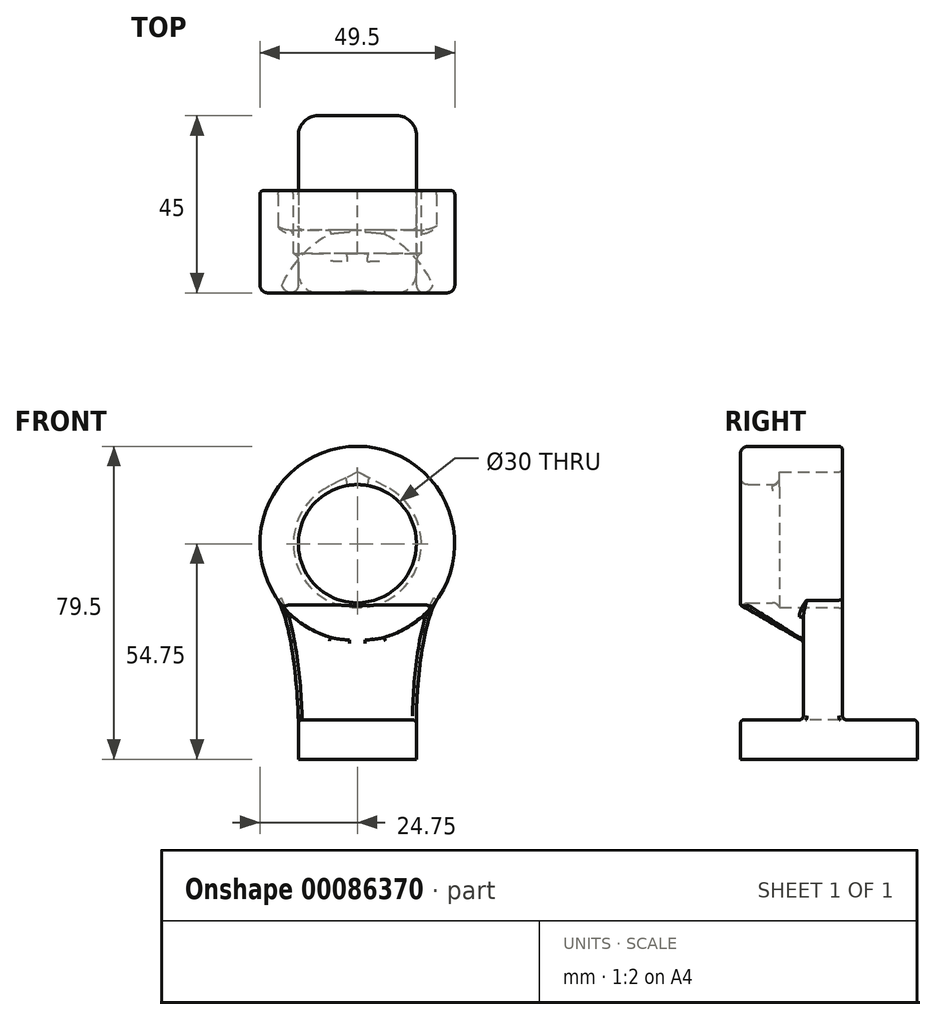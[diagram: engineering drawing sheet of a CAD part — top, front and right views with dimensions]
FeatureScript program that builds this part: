
annotation { "Feature Type Name" : "Feature", "Feature Type Description" : "" }
export const myFeature = defineFeature(function(context is Context, id is Id, definition is map)
    precondition{}
    {
        {
            var Q0;
            Q0=qCreatedBy(makeId("Front.planeOp"),FACE);
            var sketch = newSketch(context, id + "F0", { "sketchPlane" : qUnion([Q0])});
            skCircle(sketch, "E0", {"center": v(0, 54.75) * mm, "radius": 24.75 * mm});
            skLineSegment(sketch, "E1", {"start": v(-15, 0) * mm, "end": v(0, 0) * mm});
            skLineSegment(sketch, "E2", {"start": v(0, 0) * mm, "end": v(15, 0) * mm});
            skLineSegment(sketch, "E3", {"start": v(15, 0) * mm, "end": v(15, 10) * mm});
            skLineSegment(sketch, "E4", {"start": v(15, 10) * mm, "end": v(-15, 10) * mm});
            skLineSegment(sketch, "E5", {"start": v(-15, 10) * mm, "end": v(-15, 0) * mm});
            skFitSpline(sketch, "E6", {"points": [v(-15, 10) * mm, v(-20.17, 40.4) * mm], "startDerivative": vector(-0.6, 19.25) * mm, "endDerivative": vector(-11.77, 21.87) * mm});
            skFitSpline(sketch, "E7", {"points": [v(15, 10) * mm, v(20.17, 40.4) * mm], "startDerivative": vector(-0.15, 19.91) * mm, "endDerivative": vector(11.86, 18.55) * mm});
            skCircle(sketch, "E8", {"center": v(0, 54.75) * mm, "radius": 40 * mm, "construction": true});
            skSolve(sketch);
        }
        {
            var Q0;
            Q0 = qSketchRegion(id + "F0", true);
            extrude(context, id + "F1", {"entities" : qUnion([Q0]), "oppositeDirection" : true, "depth" : 10 * mm, "offsetDistance" : 25 * mm});
        }
        {
            var Q0;
            {var subQ0=sQuery(id+"F0.wireOp",EDGE,"E0");var subQ1=makeQuery(id+"F0.imprint","INTERSECT",VERTEX,{"derivedFrom":[subQ0,sQuery(id+"F0.wireOp",EDGE,"E6")]});Q0=makeQuery(id+"F0.imprint","IMPRINT",FACE,{"disambiguationData":[TD([[makeQuery(id+"F0.imprint","IMPRINT",EDGE,{"disambiguationData":[TD([[subQ1,-1.0]])],"derivedFrom":subQ0}),1.0]])]});}
            var Q1;
            Q1=makeQuery(id+"F0.imprint","IMPRINT",FACE,{"disambiguationData":[TD([[makeQuery(id+"F0.imprint","IMPRINT",EDGE,{"derivedFrom":sQuery(id+"F0.wireOp",EDGE,"E1")}),1.0]])]});
            extrude(context, id + "F2", {"entities" : qUnion([Q0, Q1]), "operationType" : NewBodyOperationType.ADD, "depth" : 16 * mm, "offsetDistance" : 25 * mm});
        }
        {
            var Q0;
            {var subQ0=sQuery(id+"F0.wireOp",EDGE,"E3");Q0=makeQuery(id+"F2.boolean.opBoolean","MERGE",FACE,{"derivedFrom":[makeQuery(id+"F1.opExtrude","SWEPT_FACE",FACE,{"disambiguationData":[OSD([subQ0])]}),makeQuery(id+"F2.opExtrude","SWEPT_FACE",FACE,{"disambiguationData":[OSD([subQ0])]})]});}
            var sketch = newSketch(context, id + "F3", { "sketchPlane" : qUnion([Q0])});
            skLineSegment(sketch, "E9.0", {"start": v(-16, 30) * mm, "end": v(-16, 79.5) * mm});
            skLineSegment(sketch, "E10.0", {"start": v(0, 30) * mm, "end": v(0, 79.5) * mm});
            skLineSegment(sketch, "E11", {"start": v(0, 30) * mm, "end": v(-16, 39.24) * mm});
            skLineSegment(sketch, "E12.0", {"start": v(-16, 10) * mm, "end": v(0, 10) * mm});
            skLineSegment(sketch, "E13", {"start": v(-16, 30) * mm, "end": v(0, 30) * mm});
            skSolve(sketch);
        }
        {
            var Q0;
            {var subQ2=sQuery(id+"F3.wireOp",EDGE,"E11");Q0=makeQuery(id+"F3.imprint","IMPRINT",FACE,{"disambiguationData":[TD([[makeQuery(id+"F3.imprint","IMPRINT",EDGE,{"derivedFrom":subQ2}),1.0]])]});}
            extrude(context, id + "F4", {"entities" : qUnion([Q0]), "operationType" : NewBodyOperationType.REMOVE, "endBound" : BoundingType.THROUGH_ALL, "oppositeDirection" : true, "depth" : 25 * mm, "offsetDistance" : 25 * mm, "hasSecondDirection" : true, "secondDirectionBound" : SecondDirectionBoundingType.THROUGH_ALL, "secondDirectionOppositeDirection" : false, "secondDirectionDepth" : 25 * mm});
        }
        {
            var Q0;
            Q0=makeQuery(id+"F1.opExtrude","CAP_FACE",FACE,{"disambiguationData":[OSD([sQuery(id+"F0.wireOp",EDGE,"E0"),sQuery(id+"F0.wireOp",EDGE,"E1"),sQuery(id+"F0.wireOp",EDGE,"E2"),sQuery(id+"F0.wireOp",EDGE,"E3"),sQuery(id+"F0.wireOp",EDGE,"E5"),sQuery(id+"F0.wireOp",EDGE,"E6"),sQuery(id+"F0.wireOp",EDGE,"E7")])],"isStart":false});
            var sketch = newSketch(context, id + "F5", { "sketchPlane" : qUnion([Q0])});
            skCircle(sketch, "E14", {"center": v(0, 54.75) * mm, "radius": 15 * mm});
            skSolve(sketch);
        }
        {
            var Q0;
            Q0 = qSketchRegion(id + "F5", true);
            extrude(context, id + "F6", {"entities" : qUnion([Q0]), "operationType" : NewBodyOperationType.REMOVE, "endBound" : BoundingType.THROUGH_ALL, "oppositeDirection" : true, "depth" : 25 * mm, "offsetDistance" : 25 * mm});
        }
        {
            var Q0;
            Q0=makeQuery(id+"F1.opExtrude","CAP_FACE",FACE,{"disambiguationData":[OSD([sQuery(id+"F0.wireOp",EDGE,"E0"),sQuery(id+"F0.wireOp",EDGE,"E1"),sQuery(id+"F0.wireOp",EDGE,"E2"),sQuery(id+"F0.wireOp",EDGE,"E3"),sQuery(id+"F0.wireOp",EDGE,"E5"),sQuery(id+"F0.wireOp",EDGE,"E6"),sQuery(id+"F0.wireOp",EDGE,"E7")])],"isStart":false});
            var sketch = newSketch(context, id + "F7", { "sketchPlane" : qUnion([Q0])});
            skArc(sketch, "E15", {"start": v(-7.4, 69.22) * mm, "mid": v(0, 38.5) * mm, "end": v(7.4, 69.22) * mm});
            skLineSegment(sketch, "E16", {"start": v(-7.4, 69.22) * mm, "end": v(0, 73) * mm});
            skLineSegment(sketch, "E17", {"start": v(0, 73) * mm, "end": v(7.4, 69.22) * mm});
            skSolve(sketch);
        }
        {
            var Q0;
            Q0 = qSketchRegion(id + "F7", true);
            extrude(context, id + "F8", {"entities" : qUnion([Q0]), "operationType" : NewBodyOperationType.REMOVE, "oppositeDirection" : true, "depth" : 16 * mm, "offsetDistance" : 25 * mm});
        }
        {
            var Q0;
            Q0=makeQuery(id+"F4.boolean.opBoolean","COPY",EDGE,{"derivedFrom":makeQuery(id+"F4.opExtrude","SWEPT_EDGE",EDGE,{"disambiguationData":[OSD([sQuery(id+"F3.wireOp",EDGE,"E9.0"),sQuery(id+"F3.wireOp",EDGE,"E11")])]})});
            var Q1;
            Q1=makeQuery(id+"F2.opExtrude","CAP_EDGE",EDGE,{"disambiguationData":[OSD([sQuery(id+"F0.wireOp",EDGE,"E0")])],"isStart":false});
            var Q2;
            {var subQ0=sQuery(id+"F0.wireOp",EDGE,"E0");Q2=makeQuery(id+"F4.boolean.opBoolean","INTERSECT",EDGE,{"disambiguationData":[OD(1.0)],"derivedFrom":[makeQuery(id+"F2.boolean.opBoolean","MERGE",FACE,{"derivedFrom":[makeQuery(id+"F1.opExtrude","SWEPT_FACE",FACE,{"disambiguationData":[OSD([subQ0])]}),makeQuery(id+"F2.opExtrude","SWEPT_FACE",FACE,{"disambiguationData":[OSD([subQ0])]})]}),makeQuery(id+"F4.opExtrude","SWEPT_FACE",FACE,{"disambiguationData":[OSD([sQuery(id+"F3.wireOp",EDGE,"E11")])]})]});}
            var Q3;
            Q3=makeQuery(id+"F6.boolean.opBoolean","COPY",FACE,{"derivedFrom":makeQuery(id+"F6.opExtrude","SWEPT_FACE",FACE,{"disambiguationData":[OSD([sQuery(id+"F5.wireOp",EDGE,"E14")])]})});
            fillet(context, id + "F9", {"entities" : qUnion([Q0, Q1, Q2, Q3]), "radius" : 2 * mm, "tangentPropagation" : true, "allowEdgeOverflow" : false});
        }
        {
            var Q0;
            Q0=makeQuery(id+"F2.opExtrude","CAP_FACE",FACE,{"disambiguationData":[OSD([sQuery(id+"F0.wireOp",EDGE,"E1"),sQuery(id+"F0.wireOp",EDGE,"E2"),sQuery(id+"F0.wireOp",EDGE,"E3"),sQuery(id+"F0.wireOp",EDGE,"E4"),sQuery(id+"F0.wireOp",EDGE,"E5")])],"isStart":false});
            extrude(context, id + "F10", {"entities" : qUnion([Q0]), "operationType" : NewBodyOperationType.ADD, "oppositeDirection" : true, "depth" : 45 * mm, "offsetDistance" : 25 * mm});
        }
        {
            var Q0;
            Q0=makeQuery(id+"F2.opExtrude","CAP_EDGE",EDGE,{"disambiguationData":[OSD([sQuery(id+"F0.wireOp",EDGE,"E3")])],"isStart":false});
            var Q1;
            Q1=makeQuery(id+"F10.opExtrude","CAP_EDGE",EDGE,{"disambiguationData":[OSD([sQuery(id+"F0.wireOp",EDGE,"E3")])],"isStart":false});
            var Q2;
            Q2=makeQuery(id+"F10.opExtrude","CAP_EDGE",EDGE,{"disambiguationData":[OSD([sQuery(id+"F0.wireOp",EDGE,"E5")])],"isStart":false});
            var Q3;
            Q3=makeQuery(id+"F2.opExtrude","CAP_EDGE",EDGE,{"disambiguationData":[OSD([sQuery(id+"F0.wireOp",EDGE,"E5")])],"isStart":false});
            fillet(context, id + "F11", {"entities" : qUnion([Q0, Q1, Q2, Q3]), "radius" : 5 * mm, "tangentPropagation" : true, "allowEdgeOverflow" : false});
        }
        {
            var Q0;
            Q0=makeQuery(id+"F1.opExtrude","CAP_FACE",FACE,{"disambiguationData":[OSD([sQuery(id+"F0.wireOp",EDGE,"E0"),sQuery(id+"F0.wireOp",EDGE,"E1"),sQuery(id+"F0.wireOp",EDGE,"E2"),sQuery(id+"F0.wireOp",EDGE,"E3"),sQuery(id+"F0.wireOp",EDGE,"E5"),sQuery(id+"F0.wireOp",EDGE,"E6"),sQuery(id+"F0.wireOp",EDGE,"E7")])],"isStart":false});
            var Q1;
            Q1=makeQuery(id+"F2.opExtrude","SWEPT_FACE",FACE,{"disambiguationData":[OSD([sQuery(id+"F0.wireOp",EDGE,"E4")])]});
            var Q2;
            Q2=makeQuery(id+"F10.opExtrude","SWEPT_FACE",FACE,{"disambiguationData":[OSD([sQuery(id+"F0.wireOp",EDGE,"E4")])]});
            var Q3;
            Q3=makeQuery(id+"F1.opExtrude","CAP_FACE",FACE,{"disambiguationData":[OSD([sQuery(id+"F0.wireOp",EDGE,"E0"),sQuery(id+"F0.wireOp",EDGE,"E1"),sQuery(id+"F0.wireOp",EDGE,"E2"),sQuery(id+"F0.wireOp",EDGE,"E3"),sQuery(id+"F0.wireOp",EDGE,"E5"),sQuery(id+"F0.wireOp",EDGE,"E6"),sQuery(id+"F0.wireOp",EDGE,"E7")])],"isStart":true});
            fillet(context, id + "F12", {"entities" : qUnion([Q0, Q1, Q2, Q3]), "radius" : 1 * mm, "tangentPropagation" : true, "allowEdgeOverflow" : false});
        }
    });
